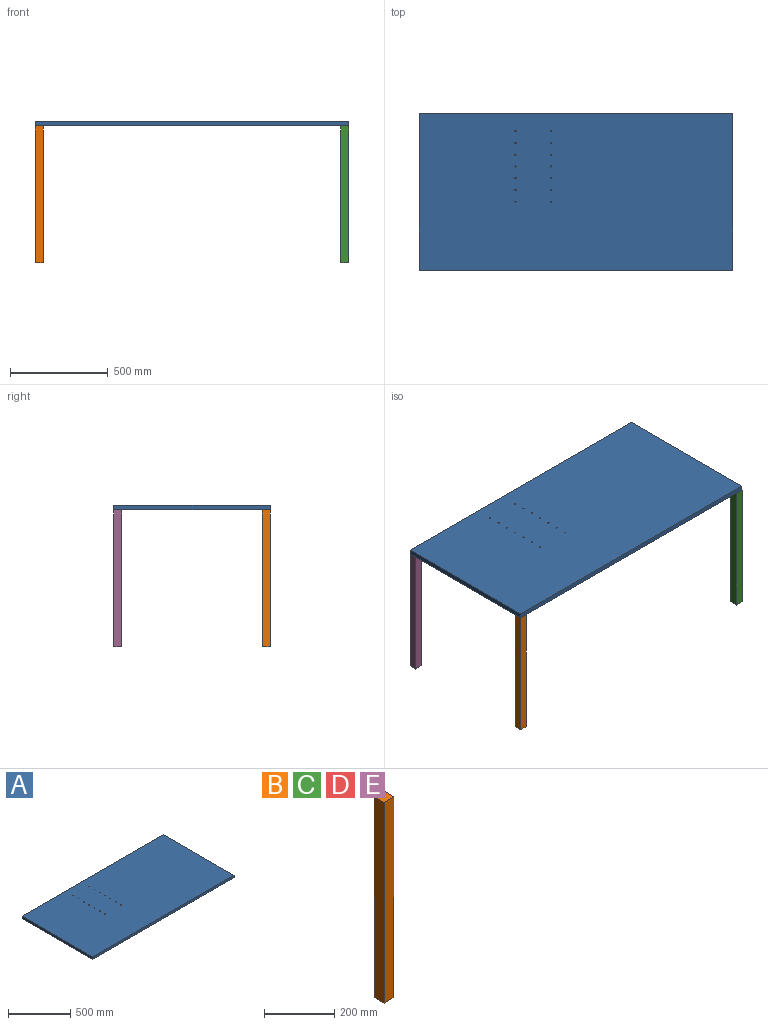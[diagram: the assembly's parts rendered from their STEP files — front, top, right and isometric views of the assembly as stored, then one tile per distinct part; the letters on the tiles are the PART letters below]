
ASSEMBLY  parts=5 mates=12
PART A: 20 faces, bbox 1600x800x25 mm
  f0: cylinder r=3.25mm len=25mm, axis (0,0,1), area 510.5mm2, adj f17,f18
  f1: cylinder r=3.25mm len=25mm, axis (0,0,1), area 510.5mm2, adj f17,f18
  f2: cylinder r=3.25mm len=25mm, axis (0,0,1), area 510.5mm2, adj f17,f18
  f3: cylinder r=3.25mm len=25mm, axis (0,0,1), area 510.5mm2, adj f17,f18
  f4: cylinder r=3.25mm len=25mm, axis (0,0,1), area 510.5mm2, adj f17,f18
  f5: cylinder r=3.25mm len=25mm, axis (0,0,1), area 510.5mm2, adj f17,f18
  f6: cylinder r=3.25mm len=25mm, axis (0,0,1), area 510.5mm2, adj f17,f18
  f7: cylinder r=3.25mm len=25mm, axis (0,0,1), area 510.5mm2, adj f17,f18
  f8: cylinder r=3.25mm len=25mm, axis (0,0,1), area 510.5mm2, adj f17,f18
  f9: cylinder r=3.25mm len=25mm, axis (0,0,1), area 510.5mm2, adj f17,f18
  f10: cylinder r=3.25mm len=25mm, axis (0,0,1), area 510.5mm2, adj f17,f18
  f11: cylinder r=3.25mm len=25mm, axis (0,0,1), area 510.5mm2, adj f17,f18
  f12: cylinder r=3.25mm len=25mm, axis (0,0,1), area 510.5mm2, adj f17,f18
  f13: plane 1600x25mm, normal (0,1,0), area 40000mm2, adj f14,f16,f17,f18
  f14: plane 800x25mm, normal (-1,0,0), area 20000mm2, adj f13,f15,f17,f18
  f15: plane 1600x25mm, normal (0,-1,0), area 40000mm2, adj f14,f16,f17,f18
  f16: plane 800x25mm, normal (1,0,0), area 20000mm2, adj f13,f15,f17,f18
  f17: plane 1600x800mm, normal (0,0,1), area 1279535.4mm2, adj f0,f1,f2,f3,f4,f5,f6,f7
  f18: plane 1600x800mm, normal (0,0,-1), area 1279535.4mm2, adj f0,f1,f2,f3,f4,f5,f6,f7
  f19: cylinder r=3.25mm len=25mm, axis (0,0,1), area 510.5mm2, adj f17,f18
PART B: 6 faces, bbox 40x40x700 mm
  f0: plane 700x40mm, normal (0,1,0), area 28000mm2, adj f1,f3,f4,f5
  f1: plane 700x40mm, normal (-1,0,0), area 28000mm2, adj f0,f2,f4,f5
  f2: plane 700x40mm, normal (0,-1,0), area 28000mm2, adj f1,f3,f4,f5
  f3: plane 700x40mm, normal (1,0,0), area 28000mm2, adj f0,f2,f4,f5
  f4: plane 40x40mm, normal (0,0,1), area 1600mm2, adj f0,f1,f2,f3
  f5: plane 40x40mm, normal (0,0,-1), area 1600mm2, adj f0,f1,f2,f3
PART C: same geometry as B
PART D: same geometry as B
PART E: same geometry as B
PLACE A t=(-349.8,353.44,538.48)mm
PLACE B t=(-1122.54,-102.89,-161.52)mm
PLACE C t=(437.46,-102.89,-161.52)mm
PLACE D t=(437.46,657.11,-161.52)mm
PLACE E t=(-1122.54,657.11,-161.52)mm
MATE planar E.f1 <-> A.f14  axis (-1,0,0) through (-1143.75,658.31,188.48)mm
MATE planar C.f4 <-> A.f18  axis (0,0,1) through (436.25,-101.69,538.48)mm
MATE planar C.f2 <-> A.f15  axis (0,-1,0) through (436.25,-121.69,188.48)mm
MATE planar C.f4 <-> E.f4  axis (0,0,1) through (436.25,-101.69,538.48)mm
MATE planar E.f4 <-> D.f4  axis (0,0,1) through (-1123.75,658.31,538.48)mm
MATE planar B.f1 <-> A.f14  axis (-1,0,0) through (-1143.75,-101.69,188.48)mm
MATE planar D.f0 <-> A.f13  axis (0,1,0) through (436.25,678.31,188.48)mm
MATE planar E.f0 <-> A.f13  axis (0,1,0) through (-1123.75,678.31,188.48)mm
MATE planar D.f3 <-> A.f16  axis (1,0,0) through (456.25,658.31,188.48)mm
MATE planar E.f4 <-> B.f4  axis (0,0,1) through (-1123.75,658.31,538.48)mm
MATE planar C.f3 <-> A.f16  axis (1,0,0) through (456.25,-101.69,188.48)mm
MATE planar B.f2 <-> C.f2  axis (0,-1,0) through (-1123.75,-121.69,188.48)mm
